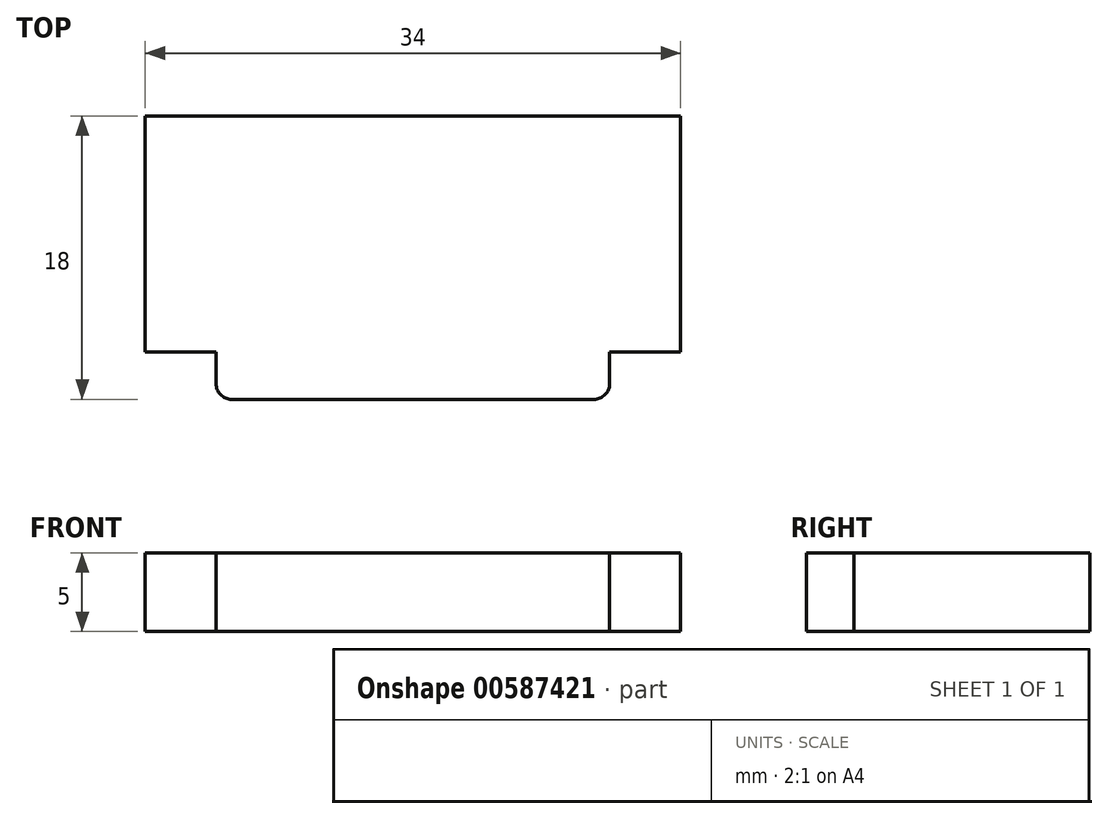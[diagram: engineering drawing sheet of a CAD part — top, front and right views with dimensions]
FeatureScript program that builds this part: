
annotation { "Feature Type Name" : "Feature", "Feature Type Description" : "" }
export const myFeature = defineFeature(function(context is Context, id is Id, definition is map)
    precondition{}
    {
        {
            var Q0;
            Q0=qCreatedBy(makeId("Top.planeOp"),FACE);
            var sketch = newSketch(context, id + "F0", { "sketchPlane" : qUnion([Q0])});
            skLineSegment(sketch, "E0", {"start": v(-17, 15) * mm, "end": v(17, 15) * mm});
            skLineSegment(sketch, "E1", {"start": v(17, 15) * mm, "end": v(17, 0) * mm});
            skLineSegment(sketch, "E2", {"start": v(17, 0) * mm, "end": v(12.5, 0) * mm});
            skLineSegment(sketch, "E3", {"start": v(12.5, 0) * mm, "end": v(12.5, -3) * mm});
            skLineSegment(sketch, "E4", {"start": v(12.5, -3) * mm, "end": v(-12.5, -3) * mm});
            skLineSegment(sketch, "E5", {"start": v(-12.5, -3) * mm, "end": v(-12.5, 0) * mm});
            skLineSegment(sketch, "E6", {"start": v(-12.5, 0) * mm, "end": v(-17, 0) * mm});
            skLineSegment(sketch, "E7", {"start": v(-17, 0) * mm, "end": v(-17, 15) * mm});
            skSolve(sketch);
        }
        {
            var Q0;
            Q0=makeQuery(id+"F0.imprint","IMPRINT",FACE,{"disambiguationData":[TD([[makeQuery(id+"F0.imprint","IMPRINT",EDGE,{"derivedFrom":sQuery(id+"F0.wireOp",EDGE,"E0")}),-1.0]])]});
            extrude(context, id + "F1", {"entities" : qUnion([Q0]), "depth" : 5 * mm, "offsetDistance" : 25 * mm});
        }
        {
            var Q0;
            Q0=makeQuery(id+"F1.opExtrude","SWEPT_EDGE",EDGE,{"disambiguationData":[OSD([sQuery(id+"F0.wireOp",EDGE,"E4"),sQuery(id+"F0.wireOp",EDGE,"E5")])]});
            var Q1;
            Q1=makeQuery(id+"F1.opExtrude","SWEPT_EDGE",EDGE,{"disambiguationData":[OSD([sQuery(id+"F0.wireOp",EDGE,"E3"),sQuery(id+"F0.wireOp",EDGE,"E4")])]});
            fillet(context, id + "F2", {"entities" : qUnion([Q0, Q1]), "radius" : 1 * mm, "tangentPropagation" : true, "allowEdgeOverflow" : false});
        }
    });
